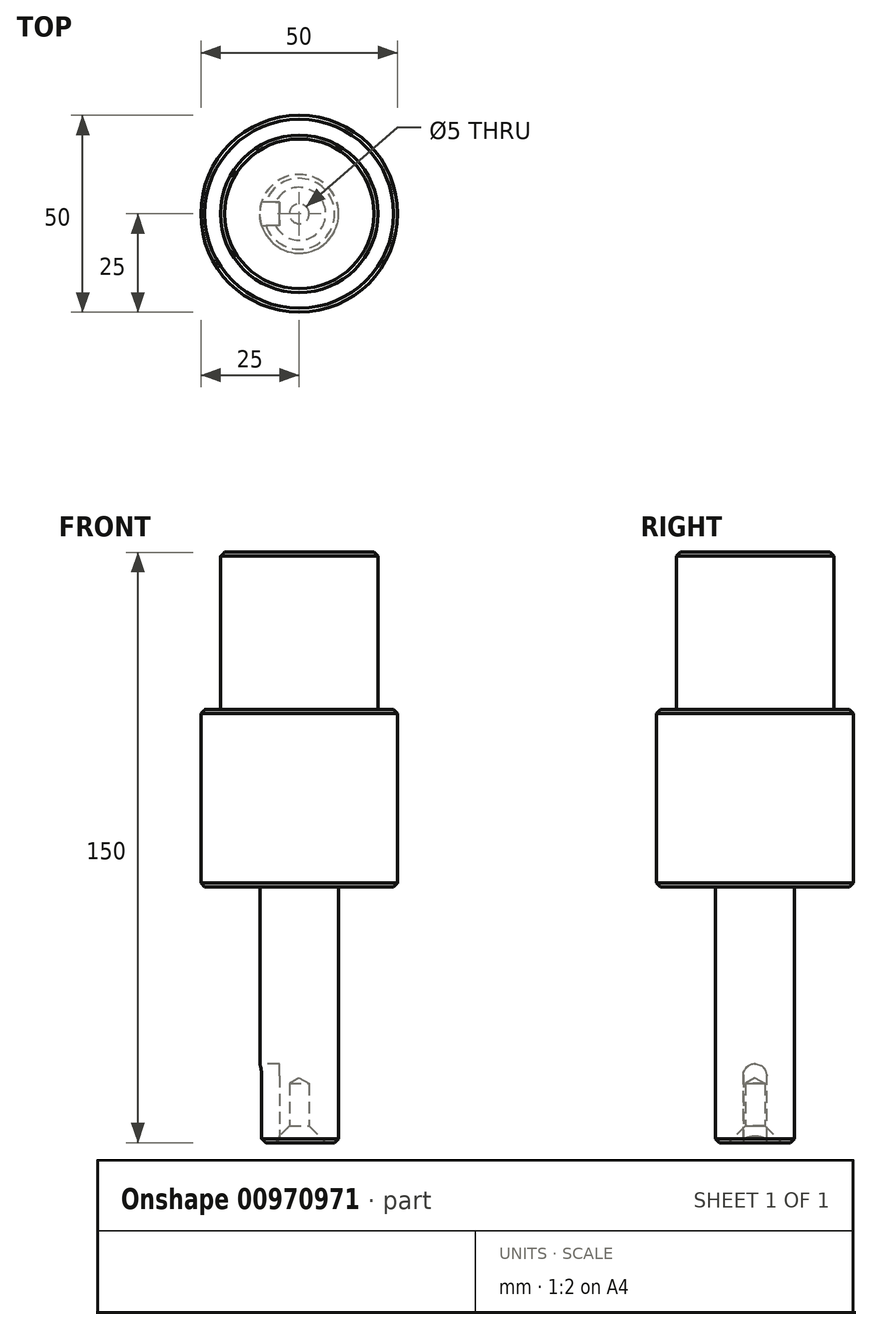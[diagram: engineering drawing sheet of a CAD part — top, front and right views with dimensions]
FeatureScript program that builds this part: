
annotation { "Feature Type Name" : "Feature", "Feature Type Description" : "" }
export const myFeature = defineFeature(function(context is Context, id is Id, definition is map)
    precondition{}
    {
        {
            var Q0;
            Q0=qCreatedBy(makeId("Front.planeOp"),FACE);
            var sketch = newSketch(context, id + "F0", { "sketchPlane" : qUnion([Q0])});
            skLineSegment(sketch, "E0", {"start": v(0, -31) * mm, "end": v(-10, -31) * mm});
            skLineSegment(sketch, "E1", {"start": v(-10, -31) * mm, "end": v(-10, 34) * mm});
            skLineSegment(sketch, "E2", {"start": v(-10, 34) * mm, "end": v(-25, 34) * mm});
            skLineSegment(sketch, "E3", {"start": v(-25, 34) * mm, "end": v(-25, 79) * mm});
            skLineSegment(sketch, "E4", {"start": v(-25, 79) * mm, "end": v(-20, 79) * mm});
            skLineSegment(sketch, "E5", {"start": v(-20, 79) * mm, "end": v(-20, 119) * mm});
            skLineSegment(sketch, "E6", {"start": v(-20, 119) * mm, "end": v(0, 119) * mm});
            skLineSegment(sketch, "E7", {"start": v(0, 119) * mm, "end": v(0, -31) * mm});
            skSolve(sketch);
        }
        {
            var Q0;
            Q0=makeQuery(id+"F0.imprint","IMPRINT",FACE,{"disambiguationData":[TD([[makeQuery(id+"F0.imprint","IMPRINT",EDGE,{"derivedFrom":sQuery(id+"F0.wireOp",EDGE,"E0")}),-1.0]])]});
            var Q1;
            Q1=sQuery(id+"F0.wireOp",EDGE,"E7");
            revolve(context, id + "F1", {"surfaceOperationType" : NewSurfaceOperationType.NEW, "entities" : qUnion([Q0]), "axis" : qUnion([Q1]), "revolveType" : RevolveType.FULL});
        }
        {
            var Q0;
            Q0=makeQuery(id+"F1.opRevolve","SWEPT_FACE",FACE,{"disambiguationData":[OSD([sQuery(id+"F0.wireOp",EDGE,"E0")])]});
            var Q1;
            Q1=makeQuery(id+"F1.opRevolve","SWEPT_EDGE",EDGE,{"disambiguationData":[OSD([sQuery(id+"F0.wireOp",EDGE,"E2"),sQuery(id+"F0.wireOp",EDGE,"E3")])]});
            var Q2;
            Q2=makeQuery(id+"F1.opRevolve","SWEPT_EDGE",EDGE,{"disambiguationData":[OSD([sQuery(id+"F0.wireOp",EDGE,"E3"),sQuery(id+"F0.wireOp",EDGE,"E4")])]});
            var Q3;
            Q3=makeQuery(id+"F1.opRevolve","SWEPT_EDGE",EDGE,{"disambiguationData":[OSD([sQuery(id+"F0.wireOp",EDGE,"E5"),sQuery(id+"F0.wireOp",EDGE,"E6")])]});
            chamfer(context, id + "F2", {"entities" : qUnion([Q0, Q1, Q2, Q3]), "width" : 1 * mm, "tangentPropagation" : true});
        }
        {
            var Q0;
            Q0=qCreatedBy(makeId("Right.planeOp"),FACE);
            cPlane(context, id + "F3", {"entities" : qUnion([Q0]), "cplaneType" : CPlaneType.OFFSET, "offset" : 10 * mm, "oppositeDirection" : true, "width" : 150 * mm, "height" : 150 * mm});
        }
        {
            var Q0;
            Q0=qCreatedBy(id+"F3.planeOp",FACE);
            var sketch = newSketch(context, id + "F4", { "sketchPlane" : qUnion([Q0])});
            skLineSegment(sketch, "E8", {"start": v(3, -31) * mm, "end": v(3, -14) * mm});
            skLineSegment(sketch, "E9", {"start": v(0, -11) * mm, "end": v(0, -11) * mm});
            skLineSegment(sketch, "E10", {"start": v(-3, -14) * mm, "end": v(-3, -31) * mm});
            skLineSegment(sketch, "E11", {"start": v(-3, -31) * mm, "end": v(3, -31) * mm});
            skPoint(sketch, "E12.visualSharp", {"position": v(3, -11) * mm});
            skArc(sketch, "E12.filletArc", {"start": v(3, -14) * mm, "mid": v(2.12, -11.89) * mm, "end": v(0, -11) * mm});
            skPoint(sketch, "E13.visualSharp", {"position": v(-3, -11) * mm});
            skArc(sketch, "E13.filletArc", {"start": v(0, -11) * mm, "mid": v(-2.12, -11.89) * mm, "end": v(-3, -14) * mm});
            skSolve(sketch);
        }
        {
            var Q0;
            Q0=makeQuery(id+"F4.imprint","IMPRINT",FACE,{"disambiguationData":[TD([[makeQuery(id+"F4.imprint","IMPRINT",EDGE,{"derivedFrom":sQuery(id+"F4.wireOp",EDGE,"E8")}),1.0]])]});
            extrude(context, id + "F5", {"entities" : qUnion([Q0]), "operationType" : NewBodyOperationType.REMOVE, "depth" : 5 * mm, "offsetDistance" : 25 * mm});
        }
        {
            var Q0;
            Q0=makeQuery(id+"F1.opRevolve","SWEPT_FACE",FACE,{"disambiguationData":[OSD([sQuery(id+"F0.wireOp",EDGE,"E0")])]});
            cPlane(context, id + "F6", {"entities" : qUnion([Q0]), "cplaneType" : CPlaneType.OFFSET, "offset" : 0 * mm, "width" : 150 * mm, "height" : 150 * mm});
        }
        {
            var Q0;
            Q0=qCreatedBy(id+"F6.planeOp",FACE);
            var sketch = newSketch(context, id + "F7", { "sketchPlane" : qUnion([Q0])});
            skPoint(sketch, "E14", {"position": v(0, 0) * mm});
            skSolve(sketch);
        }
        {
            var Q0;
            Q0=sQuery(id+"F7.wireOp",VERTEX,"E14");
            var Q1;
            Q1=makeQuery(id+"F1.opRevolve","SWEPT_BODY",BODY,{"disambiguationData":[OSD([sQuery(id+"F0.wireOp",EDGE,"E0"),sQuery(id+"F0.wireOp",EDGE,"E1"),sQuery(id+"F0.wireOp",EDGE,"E2"),sQuery(id+"F0.wireOp",EDGE,"E3"),sQuery(id+"F0.wireOp",EDGE,"E4"),sQuery(id+"F0.wireOp",EDGE,"E5"),sQuery(id+"F0.wireOp",EDGE,"E6"),sQuery(id+"F0.wireOp",EDGE,"E7")])]});
            hole(context, id + "F8", {"style" : HoleStyle.C_SINK, "endStyle" : HoleEndStyle.BLIND, "standardTappedOrClearance" : lookupTablePath({ "standard" : "ISO", "engagement" : "75%", "pitch" : "1 mm", "size" : "M6", "type" : "Tapped" }), "standardBlindInLast" : lookupTablePath({ "standard" : "ISO", "fit" : "Normal", "engagement" : "75%", "pitch" : "1 mm", "size" : "M6", "type" : "Clearance & tapped" }), "holeDiameter" : 5 * mm, "cSinkDiameter" : 13.44 * mm, "cSinkAngle" : 90 * degree, "majorDiameter" : 6 * mm, "showTappedDepth" : true, "holeDepth" : 15 * mm, "isTappedThrough" : true, "tappedDepth" : 12 * mm, "tapClearance" : 3, "startFromSketch" : true, "locations" : qUnion([Q0]), "scope" : qUnion([Q1])});
        }
    });
